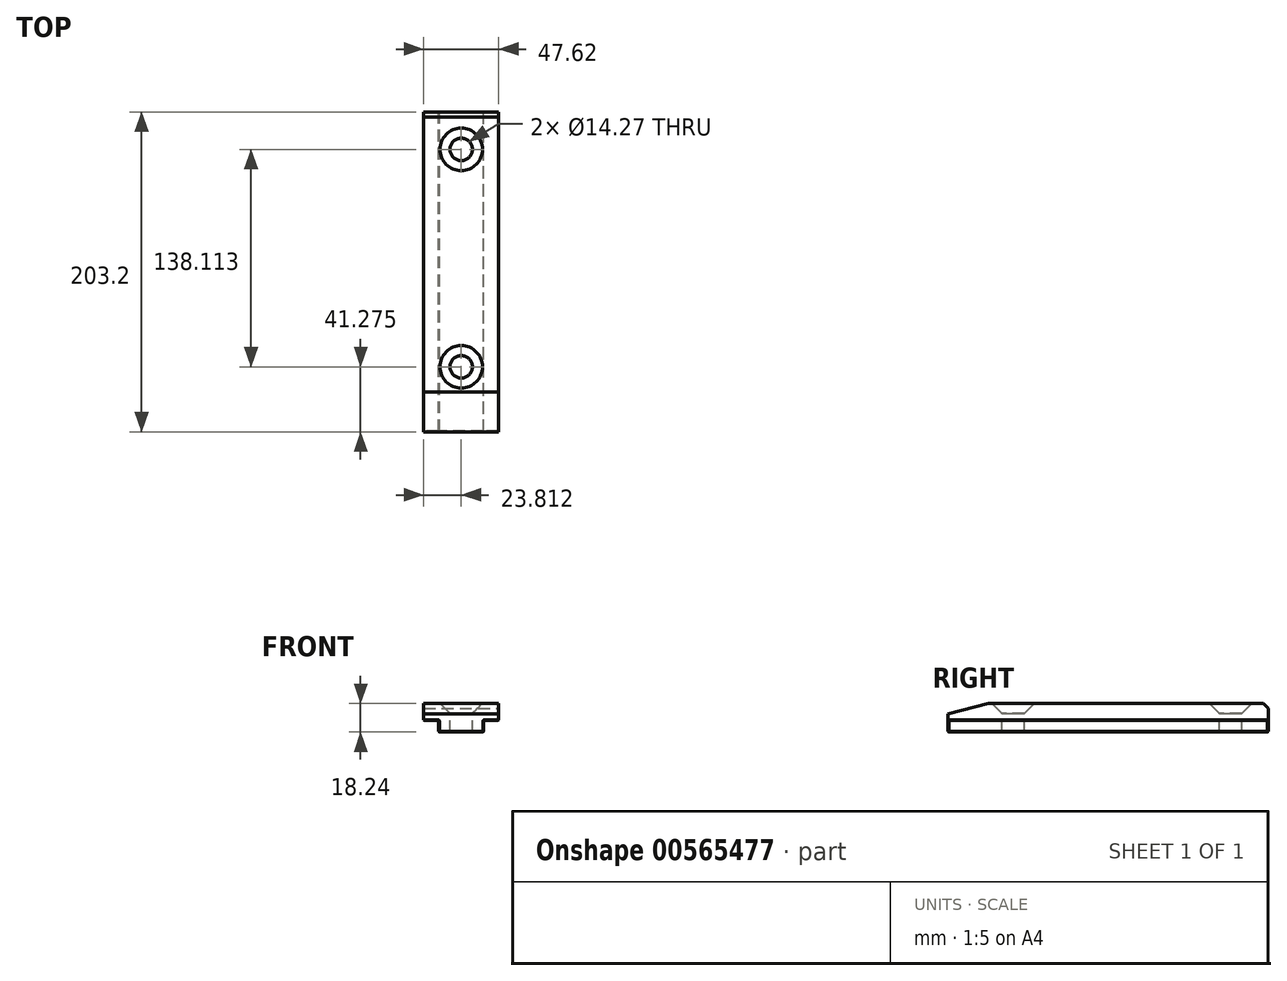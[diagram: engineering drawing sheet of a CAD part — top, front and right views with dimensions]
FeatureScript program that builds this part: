
annotation { "Feature Type Name" : "Feature", "Feature Type Description" : "" }
export const myFeature = defineFeature(function(context is Context, id is Id, definition is map)
    precondition{}
    {
        {
            var Q0;
            Q0=qCreatedBy(makeId("Front.planeOp"),FACE);
            var sketch = newSketch(context, id + "F0", { "sketchPlane" : qUnion([Q0])});
            skLineSegment(sketch, "E0", {"start": v(0, 0) * mm, "end": v(47.63, 0) * mm});
            skLineSegment(sketch, "E1", {"start": v(0, 0) * mm, "end": v(0, -10.87) * mm});
            skLineSegment(sketch, "E2.left", {"start": v(47.63, 0) * mm, "end": v(47.63, -10.87) * mm});
            skLineSegment(sketch, "E2.right", {"start": v(47.62, 0) * mm, "end": v(47.62, -10.87) * mm});
            skLineSegment(sketch, "E3", {"start": v(9.53, -18.24) * mm, "end": v(38.1, -18.24) * mm});
            skLineSegment(sketch, "E4", {"start": v(9.53, -18.24) * mm, "end": v(9.53, -10.87) * mm});
            skLineSegment(sketch, "E5", {"start": v(38.1, -18.24) * mm, "end": v(38.1, -10.87) * mm});
            skLineSegment(sketch, "E6", {"start": v(9.53, -10.87) * mm, "end": v(0, -10.87) * mm});
            skLineSegment(sketch, "E7", {"start": v(38.1, -10.87) * mm, "end": v(47.63, -10.87) * mm});
            skSolve(sketch);
        }
        {
            var Q0;
            Q0=qSketchRegion(id+"F0",true);
            extrude(context, id + "F1", {"entities" : qUnion([Q0]), "depth" : 203.2 * mm, "offsetDistance" : 25.4 * mm});
        }
        {
            var Q0;
            Q0=makeQuery(id+"F1.opExtrude","SWEPT_FACE",FACE,{"disambiguationData":[OSD([sQuery(id+"F0.wireOp",EDGE,"E1")])]});
            var sketch = newSketch(context, id + "F2", { "sketchPlane" : qUnion([Q0])});
            skLineSegment(sketch, "E8", {"start": v(203.2, 0) * mm, "end": v(177.8, 0) * mm});
            skLineSegment(sketch, "E9", {"start": v(177.8, 0) * mm, "end": v(203.2, -6.8) * mm});
            skLineSegment(sketch, "E10", {"start": v(203.2, 0) * mm, "end": v(203.2, -6.8) * mm});
            skSolve(sketch);
        }
        {
            var Q0;
            Q0=qSketchRegion(id+"F2",true);
            extrude(context, id + "F3", {"entities" : qUnion([Q0]), "operationType" : NewBodyOperationType.REMOVE, "endBound" : BoundingType.THROUGH_ALL, "oppositeDirection" : true, "depth" : 25.4 * mm, "offsetDistance" : 25.4 * mm});
        }
        {
            var Q0;
            Q0=makeQuery(id+"F1.opExtrude","SWEPT_FACE",FACE,{"disambiguationData":[OSD([sQuery(id+"F0.wireOp",EDGE,"E0")])]});
            var sketch = newSketch(context, id + "F4", { "sketchPlane" : qUnion([Q0])});
            skPoint(sketch, "E11", {"position": v(23.81, -23.81) * mm});
            skPoint(sketch, "E12", {"position": v(23.81, -161.93) * mm});
            skSolve(sketch);
        }
        {
            var Q0;
            Q0=sQuery(id+"F4.wireOp",VERTEX,"E11");
            var Q1;
            Q1=sQuery(id+"F4.wireOp",VERTEX,"E12");
            var Q2;
            Q2=makeQuery(id+"F1.opExtrude","SWEPT_BODY",BODY,{"disambiguationData":[OSD([sQuery(id+"F0.wireOp",EDGE,"E0"),sQuery(id+"F0.wireOp",EDGE,"E1"),sQuery(id+"F0.wireOp",EDGE,"E2.right"),sQuery(id+"F0.wireOp",EDGE,"E3"),sQuery(id+"F0.wireOp",EDGE,"E4"),sQuery(id+"F0.wireOp",EDGE,"E5"),sQuery(id+"F0.wireOp",EDGE,"E6"),sQuery(id+"F0.wireOp",EDGE,"E7")])]});
            hole(context, id + "F5", {"style" : HoleStyle.C_SINK, "endStyle" : HoleEndStyle.THROUGH, "holeDiameter" : 14.27 * mm, "cSinkDiameter" : 26.97 * mm, "cSinkAngle" : 90 * degree, "isTappedThrough" : true, "tappedDepth" : 1.27 * mm, "tapClearance" : 3, "startFromSketch" : true, "locations" : qUnion([Q0, Q1]), "scope" : qUnion([Q2])});
        }
        {
            var Q0;
            Q0=makeQuery(id+"F1.opExtrude","CAP_EDGE",EDGE,{"disambiguationData":[OSD([sQuery(id+"F0.wireOp",EDGE,"E0")])],"isStart":true});
            chamfer(context, id + "F6", {"entities" : qUnion([Q0]), "width" : 3.17 * mm, "tangentPropagation" : true});
        }
        {
            var Q0;
            Q0=makeQuery(id+"F1.opExtrude","SWEPT_EDGE",EDGE,{"disambiguationData":[OSD([sQuery(id+"F0.wireOp",EDGE,"E4"),sQuery(id+"F0.wireOp",EDGE,"E6")])]});
            var Q1;
            Q1=makeQuery(id+"F1.opExtrude","SWEPT_EDGE",EDGE,{"disambiguationData":[OSD([sQuery(id+"F0.wireOp",EDGE,"E5"),sQuery(id+"F0.wireOp",EDGE,"E7")])]});
            fillet(context, id + "F7", {"entities" : qUnion([Q0, Q1]), "radius" : 0.25 * mm, "tangentPropagation" : true, "allowEdgeOverflow" : false});
        }
        {
            var Q0;
            Q0=makeQuery(id+"F1.opExtrude","SWEPT_EDGE",EDGE,{"disambiguationData":[OSD([sQuery(id+"F0.wireOp",EDGE,"E3"),sQuery(id+"F0.wireOp",EDGE,"E5")])]});
            var Q1;
            Q1=makeQuery(id+"F1.opExtrude","SWEPT_EDGE",EDGE,{"disambiguationData":[OSD([sQuery(id+"F0.wireOp",EDGE,"E3"),sQuery(id+"F0.wireOp",EDGE,"E4")])]});
            var Q2;
            Q2=makeQuery(id+"F1.opExtrude","CAP_EDGE",EDGE,{"disambiguationData":[OSD([sQuery(id+"F0.wireOp",EDGE,"E3")])],"isStart":false});
            var Q3;
            Q3=makeQuery(id+"F1.opExtrude","CAP_EDGE",EDGE,{"disambiguationData":[OSD([sQuery(id+"F0.wireOp",EDGE,"E3")])],"isStart":true});
            var Q4;
            Q4=makeQuery(id+"F1.opExtrude","CAP_EDGE",EDGE,{"disambiguationData":[OSD([sQuery(id+"F0.wireOp",EDGE,"E5")])],"isStart":true});
            var Q5;
            Q5=makeQuery(id+"F1.opExtrude","CAP_EDGE",EDGE,{"disambiguationData":[OSD([sQuery(id+"F0.wireOp",EDGE,"E4")])],"isStart":true});
            var Q6;
            Q6=makeQuery(id+"F1.opExtrude","CAP_EDGE",EDGE,{"disambiguationData":[OSD([sQuery(id+"F0.wireOp",EDGE,"E4")])],"isStart":false});
            var Q7;
            Q7=makeQuery(id+"F1.opExtrude","CAP_EDGE",EDGE,{"disambiguationData":[OSD([sQuery(id+"F0.wireOp",EDGE,"E5")])],"isStart":false});
            var Q8;
            Q8=makeQuery(id+"F1.opExtrude","SWEPT_EDGE",EDGE,{"disambiguationData":[OSD([sQuery(id+"F0.wireOp",EDGE,"E2.right"),sQuery(id+"F0.wireOp",EDGE,"E7")])]});
            var Q9;
            Q9=makeQuery(id+"F1.opExtrude","SWEPT_EDGE",EDGE,{"disambiguationData":[OSD([sQuery(id+"F0.wireOp",EDGE,"E1"),sQuery(id+"F0.wireOp",EDGE,"E6")])]});
            chamfer(context, id + "F8", {"entities" : qUnion([Q0, Q1, Q2, Q3, Q4, Q5, Q6, Q7, Q8, Q9]), "width" : 0.38 * mm, "tangentPropagation" : true});
        }
    });
